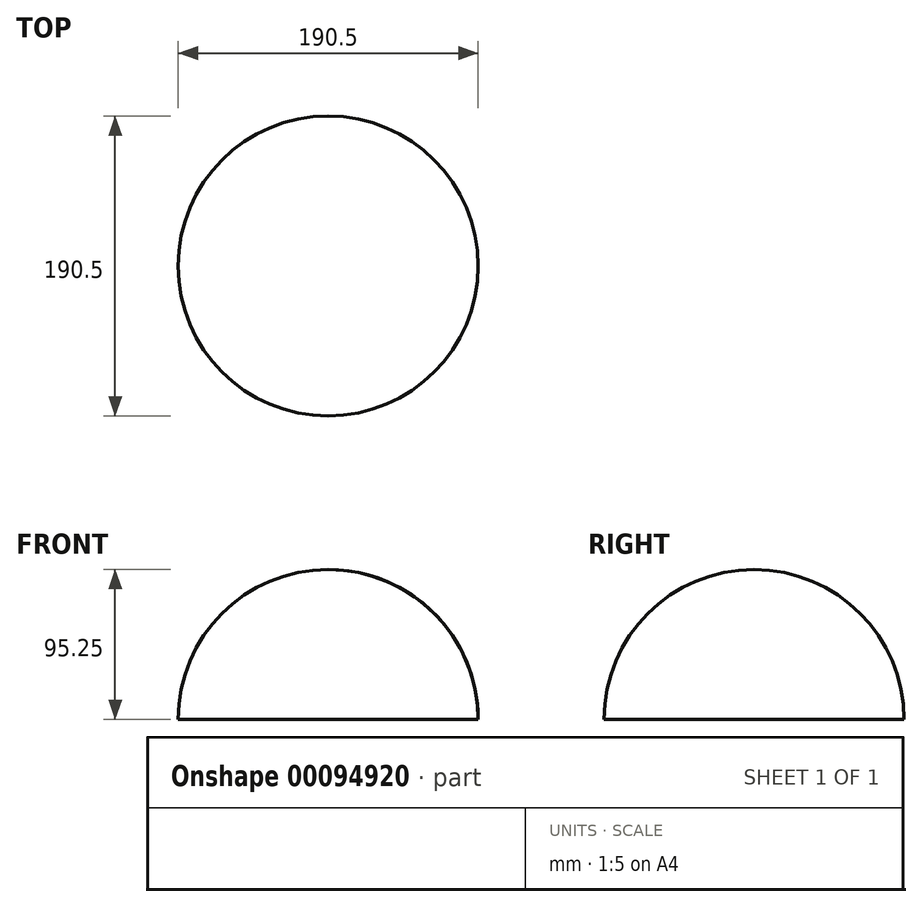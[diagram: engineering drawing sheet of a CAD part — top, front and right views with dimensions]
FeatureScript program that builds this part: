
annotation { "Feature Type Name" : "Feature", "Feature Type Description" : "" }
export const myFeature = defineFeature(function(context is Context, id is Id, definition is map)
    precondition{}
    {
        {
            var Q0;
            Q0=qCreatedBy(makeId("Front.planeOp"),FACE);
            var sketch = newSketch(context, id + "F0", { "sketchPlane" : qUnion([Q0])});
            skCircle(sketch, "E0", {"center": v(0, 0) * mm, "radius": 95.25 * mm});
            skLineSegment(sketch, "E1", {"start": v(-95.25, 0) * mm, "end": v(95.25, 0) * mm});
            skLineSegment(sketch, "E2", {"start": v(0, 0) * mm, "end": v(0, 95.25) * mm});
            skSolve(sketch);
        }
        {
            var Q0;
            {var subQ3=sQuery(id+"F0.wireOp",EDGE,"E2");Q0=makeQuery(id+"F0.imprint","IMPRINT",FACE,{"disambiguationData":[TD([[makeQuery(id+"F0.imprint","IMPRINT",EDGE,{"derivedFrom":subQ3}),-1.0]])]});}
            var Q1;
            Q1=sQuery(id+"F0.wireOp",EDGE,"E2");
            revolve(context, id + "F1", {"entities" : qUnion([Q0]), "axis" : qUnion([Q1]), "revolveType" : RevolveType.FULL});
        }
    });
